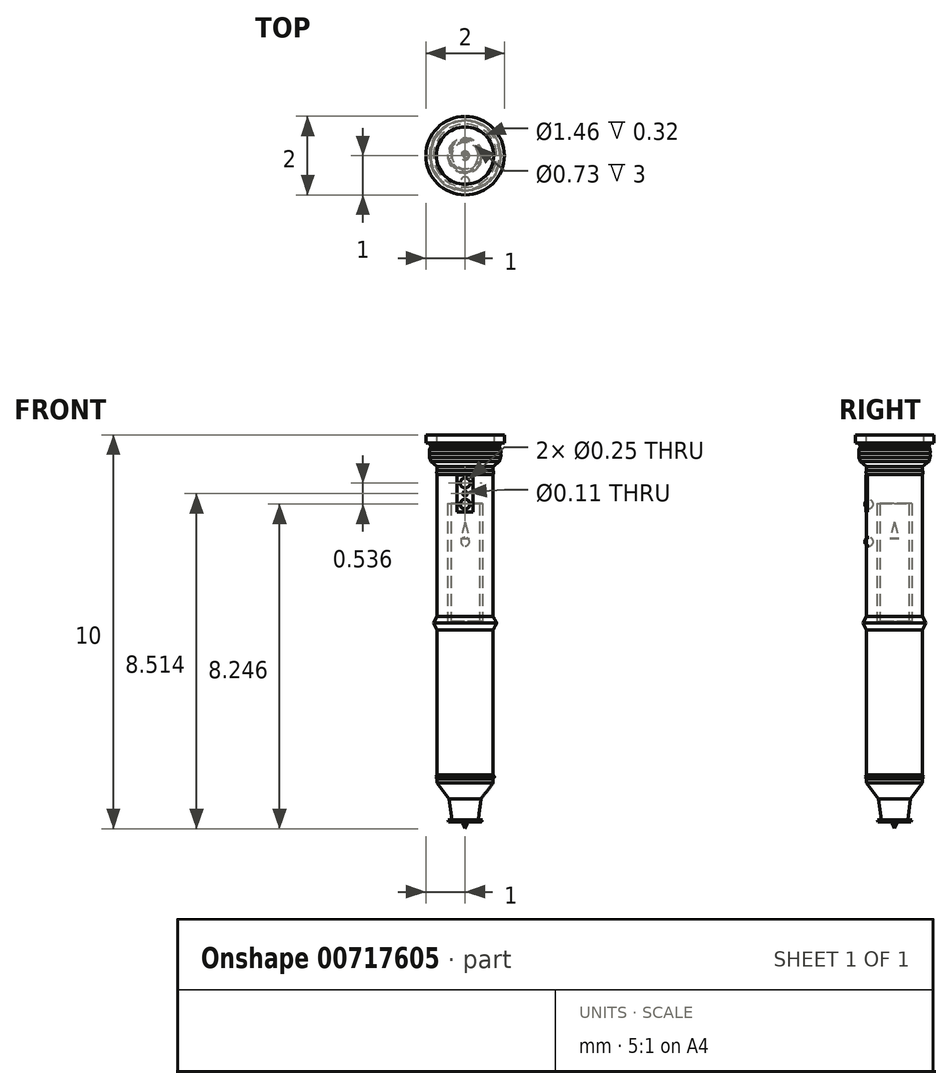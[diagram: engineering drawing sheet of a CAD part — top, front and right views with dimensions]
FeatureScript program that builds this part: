
annotation { "Feature Type Name" : "Feature", "Feature Type Description" : "" }
export const myFeature = defineFeature(function(context is Context, id is Id, definition is map)
    precondition{}
    {
        {
            var Q0;
            Q0=qCreatedBy(makeId("Front.planeOp"),FACE);
            var sketch = newSketch(context, id + "F0", { "sketchPlane" : qUnion([Q0])});
            skLineSegment(sketch, "E0", {"start": v(0, 2.08) * mm, "end": v(0, -7.92) * mm});
            skLineSegment(sketch, "E1", {"start": v(0, 2.08) * mm, "end": v(-1, 2.08) * mm});
            skLineSegment(sketch, "E2", {"start": v(-1, 2.08) * mm, "end": v(-1, 1.88) * mm});
            skLineSegment(sketch, "E3", {"start": v(-1, 1.88) * mm, "end": v(-0.9, 1.88) * mm});
            skLineSegment(sketch, "E4", {"start": v(-0.9, 1.88) * mm, "end": v(-0.87, 1.79) * mm});
            skLineSegment(sketch, "E5", {"start": v(-0.87, 1.79) * mm, "end": v(-0.9, 1.7) * mm});
            skFitSpline(sketch, "E6", {"points": [v(-0.9, 1.7) * mm, v(-0.9, 1.66) * mm, v(-0.9, 1.6) * mm], "startDerivative": vector(-0.03, -0.1) * mm, "endDerivative": vector(0.03, -0.1) * mm});
            skFitSpline(sketch, "E7", {"points": [v(-0.9, 1.6) * mm, v(-0.9, 1.56) * mm, v(-0.9, 1.51) * mm], "startDerivative": vector(-0.03, -0.1) * mm, "endDerivative": vector(0.03, -0.1) * mm});
            skLineSegment(sketch, "E8", {"start": v(-0.9, 1.51) * mm, "end": v(-0.87, 1.41) * mm});
            skLineSegment(sketch, "E9", {"start": v(-0.87, 1.41) * mm, "end": v(-0.71, 1.28) * mm});
            skLineSegment(sketch, "E10", {"start": v(-0.71, 1.28) * mm, "end": v(-0.71, -6.76) * mm});
            skLineSegment(sketch, "E11", {"start": v(-0.4, -7.16) * mm, "end": v(-0.71, -6.76) * mm});
            skFitSpline(sketch, "E12", {"points": [v(-0.71, 1.18) * mm, v(-0.72, 1.13) * mm, v(-0.71, 1.08) * mm], "startDerivative": vector(-0.03, -0.1) * mm, "endDerivative": vector(0.03, -0.1) * mm});
            skLineSegment(sketch, "E13", {"start": v(-0.71, -6.65) * mm, "end": v(-0.71, -6.55) * mm});
            skLineSegment(sketch, "E14", {"start": v(-0.71, -6.55) * mm, "end": v(-0.71, -6.6) * mm});
            skLineSegment(sketch, "E15", {"start": v(-0.71, -6.6) * mm, "end": v(-0.75, -6.6) * mm});
            skLineSegment(sketch, "E16", {"start": v(-0.75, -6.6) * mm, "end": v(-0.71, -6.55) * mm});
            skLineSegment(sketch, "E17", {"start": v(-0.75, -6.6) * mm, "end": v(-0.71, -6.65) * mm});
            skLineSegment(sketch, "E18", {"start": v(-0.33, -7.7) * mm, "end": v(-0.44, -7.7) * mm});
            skLineSegment(sketch, "E19", {"start": v(-0.44, -7.7) * mm, "end": v(-0.42, -7.75) * mm});
            skLineSegment(sketch, "E20", {"start": v(-0.42, -7.75) * mm, "end": v(0, -7.75) * mm});
            skLineSegment(sketch, "E21", {"start": v(-0.09, -7.75) * mm, "end": v(-0.09, -7.79) * mm});
            skLineSegment(sketch, "E22", {"start": v(-0.09, -7.79) * mm, "end": v(-0.06, -7.79) * mm});
            skLineSegment(sketch, "E23", {"start": v(-0.06, -7.79) * mm, "end": v(0, -7.92) * mm});
            skLineSegment(sketch, "E24", {"start": v(-0.4, -7.16) * mm, "end": v(-0.33, -7.7) * mm});
            skLineSegment(sketch, "E25", {"start": v(-0.71, -2.53) * mm, "end": v(-0.8, -2.7) * mm});
            skLineSegment(sketch, "E26", {"start": v(-0.8, -2.7) * mm, "end": v(-0.71, -2.87) * mm});
            skSolve(sketch);
        }
        {
            var Q0;
            Q0 = qSketchRegion(id + "F0", true);
            var Q1;
            Q1=sQuery(id+"F0.wireOp",EDGE,"E0");
            revolve(context, id + "F1", {"surfaceOperationType" : NewSurfaceOperationType.NEW, "entities" : qUnion([Q0]), "axis" : qUnion([Q1]), "revolveType" : RevolveType.FULL});
        }
        {
            var Q0;
            Q0=makeQuery(id+"F1.opRevolve","SWEPT_BODY",BODY,{"disambiguationData":[OSD([sQuery(id+"F0.wireOp",EDGE,"E0"),sQuery(id+"F0.wireOp",EDGE,"E1"),sQuery(id+"F0.wireOp",EDGE,"E2"),sQuery(id+"F0.wireOp",EDGE,"E3"),sQuery(id+"F0.wireOp",EDGE,"E4"),sQuery(id+"F0.wireOp",EDGE,"E5"),sQuery(id+"F0.wireOp",EDGE,"E6"),sQuery(id+"F0.wireOp",EDGE,"E7"),sQuery(id+"F0.wireOp",EDGE,"E8"),sQuery(id+"F0.wireOp",EDGE,"E9"),sQuery(id+"F0.wireOp",EDGE,"E10"),sQuery(id+"F0.wireOp",EDGE,"E11"),sQuery(id+"F0.wireOp",EDGE,"E12"),sQuery(id+"F0.wireOp",EDGE,"E16"),sQuery(id+"F0.wireOp",EDGE,"E17"),sQuery(id+"F0.wireOp",EDGE,"E18"),sQuery(id+"F0.wireOp",EDGE,"E19"),sQuery(id+"F0.wireOp",EDGE,"E20"),sQuery(id+"F0.wireOp",EDGE,"E21"),sQuery(id+"F0.wireOp",EDGE,"E22"),sQuery(id+"F0.wireOp",EDGE,"E23"),sQuery(id+"F0.wireOp",EDGE,"E24")])]});
            transform(context, id + "F2", {"entities" : qUnion([Q0]), "transformType" : TransformType.TRANSLATION_3D, "dx" : 0 * mm, "dy" : 0 * mm, "dz" : -2.5 * mm, "makeCopy" : false});
        }
        {
            var Q0;
            Q0=qCreatedBy(makeId("Top.planeOp"),FACE);
            var sketch = newSketch(context, id + "F3", { "sketchPlane" : qUnion([Q0])});
            skCircle(sketch, "E27", {"center": v(0, 0) * mm, "radius": 0.91 * mm});
            skSolve(sketch);
        }
        {
            var Q0;
            Q0 = qSketchRegion(id + "F3", true);
            extrude(context, id + "F4", {"entities" : qUnion([Q0]), "depth" : 0.6 * mm, "offsetDistance" : 25 * mm});
        }
        {
            var Q0;
            Q0=makeQuery(id+"F4.opExtrude","SWEPT_BODY",BODY,{"disambiguationData":[OSD([sQuery(id+"F3.wireOp",EDGE,"E27")])]});
            transform(context, id + "F5", {"entities" : qUnion([Q0]), "transformType" : TransformType.TRANSLATION_3D, "dx" : 0 * mm, "dy" : 0 * mm, "dz" : -0.9 * mm, "makeCopy" : false});
        }
        {
            var Q0;
            Q0=makeQuery(id+"F4.opExtrude","SWEPT_BODY",BODY,{"disambiguationData":[OSD([sQuery(id+"F3.wireOp",EDGE,"E27")])]});
            var Q1;
            Q1=qCreatedBy(makeId("Origin.pointOp"),VERTEX);
            transform(context, id + "F6", {"entities" : qUnion([Q0]), "transformType" : TransformType.SCALE_UNIFORMLY, "scale" : 0.8, "scalePoint" : qUnion([Q1]), "makeCopy" : false});
        }
        {
            var Q0;
            Q0=makeQuery(id+"F4.opExtrude","SWEPT_BODY",BODY,{"disambiguationData":[OSD([sQuery(id+"F3.wireOp",EDGE,"E27")])]});
            var Q1;
            Q1=makeQuery(id+"F1.opRevolve","SWEPT_BODY",BODY,{"disambiguationData":[OSD([sQuery(id+"F0.wireOp",EDGE,"E0"),sQuery(id+"F0.wireOp",EDGE,"E1"),sQuery(id+"F0.wireOp",EDGE,"E2"),sQuery(id+"F0.wireOp",EDGE,"E3"),sQuery(id+"F0.wireOp",EDGE,"E4"),sQuery(id+"F0.wireOp",EDGE,"E5"),sQuery(id+"F0.wireOp",EDGE,"E6"),sQuery(id+"F0.wireOp",EDGE,"E7"),sQuery(id+"F0.wireOp",EDGE,"E8"),sQuery(id+"F0.wireOp",EDGE,"E9"),sQuery(id+"F0.wireOp",EDGE,"E10"),sQuery(id+"F0.wireOp",EDGE,"E11"),sQuery(id+"F0.wireOp",EDGE,"E12"),sQuery(id+"F0.wireOp",EDGE,"E16"),sQuery(id+"F0.wireOp",EDGE,"E17"),sQuery(id+"F0.wireOp",EDGE,"E18"),sQuery(id+"F0.wireOp",EDGE,"E19"),sQuery(id+"F0.wireOp",EDGE,"E20"),sQuery(id+"F0.wireOp",EDGE,"E21"),sQuery(id+"F0.wireOp",EDGE,"E22"),sQuery(id+"F0.wireOp",EDGE,"E23"),sQuery(id+"F0.wireOp",EDGE,"E24")])]});
            booleanBodies(context, id + "F7", {"operationType" : BooleanOperationType.SUBTRACTION, "tools" : qUnion([Q0]), "targets" : qUnion([Q1])});
        }
        {
            var Q0;
            Q0=qCreatedBy(makeId("Front.planeOp"),FACE);
            var sketch = newSketch(context, id + "F8", { "sketchPlane" : qUnion([Q0])});
            skCircle(sketch, "E28", {"center": v(0, -1.63) * mm, "radius": 0.12 * mm});
            skCircle(sketch, "E29", {"center": v(0, -2.16) * mm, "radius": 0.12 * mm});
            skCircle(sketch, "E30", {"center": v(0, -1.9) * mm, "radius": 0.06 * mm});
            skLineSegment(sketch, "E31", {"start": v(0, -2.37) * mm, "end": v(0.2, -2.37) * mm});
            skLineSegment(sketch, "E32", {"start": v(0.2, -2.37) * mm, "end": v(0.2, -1.43) * mm});
            skLineSegment(sketch, "E33", {"start": v(0.2, -1.43) * mm, "end": v(-0.2, -1.43) * mm});
            skLineSegment(sketch, "E34", {"start": v(-0.2, -1.43) * mm, "end": v(-0.2, -2.37) * mm});
            skLineSegment(sketch, "E35", {"start": v(-0.2, -2.37) * mm, "end": v(0, -2.37) * mm});
            skSolve(sketch);
        }
        {
            var Q0;
            Q0 = qSketchRegion(id + "F8", true);
            extrude(context, id + "F9", {"entities" : qUnion([Q0]), "operationType" : NewBodyOperationType.ADD, "depth" : 0.72 * mm, "offsetDistance" : 25 * mm});
        }
        {
            var Q0;
            Q0=qCreatedBy(makeId("Front.planeOp"),FACE);
            var sketch = newSketch(context, id + "F10", { "sketchPlane" : qUnion([Q0])});
            skLineSegment(sketch, "E36", {"start": v(0, -1.52) * mm, "end": v(0, -1.74) * mm});
            skFitSpline(sketch, "E37", {"points": [v(0, -1.52) * mm, v(-0.1, -1.63) * mm, v(0, -1.74) * mm], "startDerivative": vector(-0.4, 0) * mm, "endDerivative": vector(0.4, 0) * mm});
            skSolve(sketch);
        }
        {
            var Q0;
            Q0 = qSketchRegion(id + "F10", true);
            var Q1;
            Q1=sQuery(id+"F10.wireOp",EDGE,"E36");
            revolve(context, id + "F11", {"surfaceOperationType" : NewSurfaceOperationType.NEW, "entities" : qUnion([Q0]), "axis" : qUnion([Q1]), "revolveType" : RevolveType.FULL});
        }
        {
            var Q0;
            Q0=makeQuery(id+"F11.opRevolve","SWEPT_BODY",BODY,{"disambiguationData":[OSD([sQuery(id+"F10.wireOp",EDGE,"E36"),sQuery(id+"F10.wireOp",EDGE,"E37")])]});
            transform(context, id + "F12", {"entities" : qUnion([Q0]), "transformType" : TransformType.TRANSLATION_3D, "dx" : 0 * mm, "dy" : 2.07 * mm, "dz" : 0 * mm, "makeCopy" : false});
        }
        {
            var Q0;
            Q0=makeQuery(id+"F11.opRevolve","SWEPT_BODY",BODY,{"disambiguationData":[OSD([sQuery(id+"F10.wireOp",EDGE,"E36"),sQuery(id+"F10.wireOp",EDGE,"E37")])]});
            transform(context, id + "F13", {"entities" : qUnion([Q0]), "transformType" : TransformType.TRANSLATION_3D, "dx" : 0 * mm, "dy" : 0 * mm, "dz" : -0.54 * mm, "makeCopy" : true});
        }
        {
            var Q0;
            Q0=makeQuery(id+"F13.opPattern","COPY",BODY,{"derivedFrom":makeQuery(id+"F11.opRevolve","SWEPT_BODY",BODY,{"disambiguationData":[OSD([sQuery(id+"F10.wireOp",EDGE,"E36"),sQuery(id+"F10.wireOp",EDGE,"E37")])]}),"instanceName":"1"});
            var Q1;
            Q1=makeQuery(id+"F11.opRevolve","SWEPT_BODY",BODY,{"disambiguationData":[OSD([sQuery(id+"F10.wireOp",EDGE,"E36"),sQuery(id+"F10.wireOp",EDGE,"E37")])]});
            transform(context, id + "F14", {"entities" : qUnion([Q0, Q1]), "transformType" : TransformType.TRANSLATION_3D, "dx" : 0 * mm, "dy" : -2.72 * mm, "dz" : 0 * mm, "makeCopy" : false});
        }
        {
            var Q0;
            Q0=makeQuery(id+"F11.opRevolve","SWEPT_BODY",BODY,{"disambiguationData":[OSD([sQuery(id+"F10.wireOp",EDGE,"E36"),sQuery(id+"F10.wireOp",EDGE,"E37")])]});
            transform(context, id + "F15", {"entities" : qUnion([Q0]), "transformType" : TransformType.TRANSLATION_3D, "dx" : 0 * mm, "dy" : 0 * mm, "dz" : -1.49 * mm, "makeCopy" : false});
        }
        {
            var Q0;
            Q0=qCreatedBy(makeId("Top.planeOp"),FACE);
            var sketch = newSketch(context, id + "F16", { "sketchPlane" : qUnion([Q0])});
            skCircle(sketch, "E38", {"center": v(0, 0) * mm, "radius": 0.27 * mm});
            skSolve(sketch);
        }
        {
            var Q0;
            Q0 = qSketchRegion(id + "F16", true);
            extrude(context, id + "F17", {"entities" : qUnion([Q0]), "depth" : 0.8 * mm, "offsetDistance" : 25 * mm});
        }
        {
            var Q0;
            Q0=makeQuery(id+"F17.opExtrude","SWEPT_BODY",BODY,{"disambiguationData":[OSD([sQuery(id+"F16.wireOp",EDGE,"E38")])]});
            transform(context, id + "F18", {"entities" : qUnion([Q0]), "transformType" : TransformType.TRANSLATION_3D, "dx" : 0 * mm, "dy" : 0 * mm, "dz" : -2.92 * mm, "makeCopy" : false});
        }
        {
            var Q0;
            Q0=makeQuery(id+"F17.opExtrude","SWEPT_BODY",BODY,{"disambiguationData":[OSD([sQuery(id+"F16.wireOp",EDGE,"E38")])]});
            var Q1;
            Q1=makeQuery(id+"F11.opRevolve","SWEPT_BODY",BODY,{"disambiguationData":[OSD([sQuery(id+"F10.wireOp",EDGE,"E36"),sQuery(id+"F10.wireOp",EDGE,"E37")])]});
            booleanBodies(context, id + "F19", {"operationType" : BooleanOperationType.SUBTRACTION, "tools" : qUnion([Q0]), "targets" : qUnion([Q1])});
        }
        {
            var Q0;
            Q0=qCreatedBy(makeId("Top.planeOp"),FACE);
            var sketch = newSketch(context, id + "F20", { "sketchPlane" : qUnion([Q0])});
            skCircle(sketch, "E39", {"center": v(0, 0) * mm, "radius": 0.36 * mm});
            skCircle(sketch, "E40", {"center": v(0, 0) * mm, "radius": 0.45 * mm});
            skSolve(sketch);
        }
        {
            var Q0;
            Q0=makeQuery(id+"F20.imprint","IMPRINT",FACE,{"disambiguationData":[TD([[makeQuery(id+"F20.imprint","IMPRINT",EDGE,{"derivedFrom":sQuery(id+"F20.wireOp",EDGE,"E39")}),-1.0]])]});
            extrude(context, id + "F21", {"entities" : qUnion([Q0]), "depth" : 3 * mm, "offsetDistance" : 25 * mm});
        }
        {
            var Q0;
            Q0=makeQuery(id+"F21.opExtrude","SWEPT_BODY",BODY,{"disambiguationData":[OSD([sQuery(id+"F20.wireOp",EDGE,"E39"),sQuery(id+"F20.wireOp",EDGE,"E40")])]});
            transform(context, id + "F22", {"entities" : qUnion([Q0]), "transformType" : TransformType.TRANSLATION_3D, "dx" : 0 * mm, "dy" : 0 * mm, "dz" : -5.15 * mm, "makeCopy" : false});
        }
        {
            var Q0;
            Q0=qCreatedBy(makeId("Front.planeOp"),FACE);
            var sketch = newSketch(context, id + "F23", { "sketchPlane" : qUnion([Q0])});
            skLineSegment(sketch, "E41", {"start": v(0, 0) * mm, "end": v(-0.11, -0.42) * mm});
            skLineSegment(sketch, "E42", {"start": v(-0.11, -0.42) * mm, "end": v(0, -0.42) * mm});
            skLineSegment(sketch, "E43", {"start": v(0, -0.42) * mm, "end": v(0, 0) * mm});
            skSolve(sketch);
        }
        {
            var Q0;
            Q0 = qSketchRegion(id + "F23", true);
            var Q1;
            Q1=sQuery(id+"F23.wireOp",EDGE,"E43");
            revolve(context, id + "F24", {"surfaceOperationType" : NewSurfaceOperationType.NEW, "entities" : qUnion([Q0]), "axis" : qUnion([Q1]), "revolveType" : RevolveType.FULL});
        }
        {
            var Q0;
            Q0=makeQuery(id+"F24.opRevolve","SWEPT_BODY",BODY,{"disambiguationData":[OSD([sQuery(id+"F23.wireOp",EDGE,"E41"),sQuery(id+"F23.wireOp",EDGE,"E42"),sQuery(id+"F23.wireOp",EDGE,"E43")])]});
            transform(context, id + "F25", {"entities" : qUnion([Q0]), "transformType" : TransformType.TRANSLATION_3D, "dx" : 0 * mm, "dy" : 0 * mm, "dz" : -2.6 * mm, "makeCopy" : false});
        }
    });
